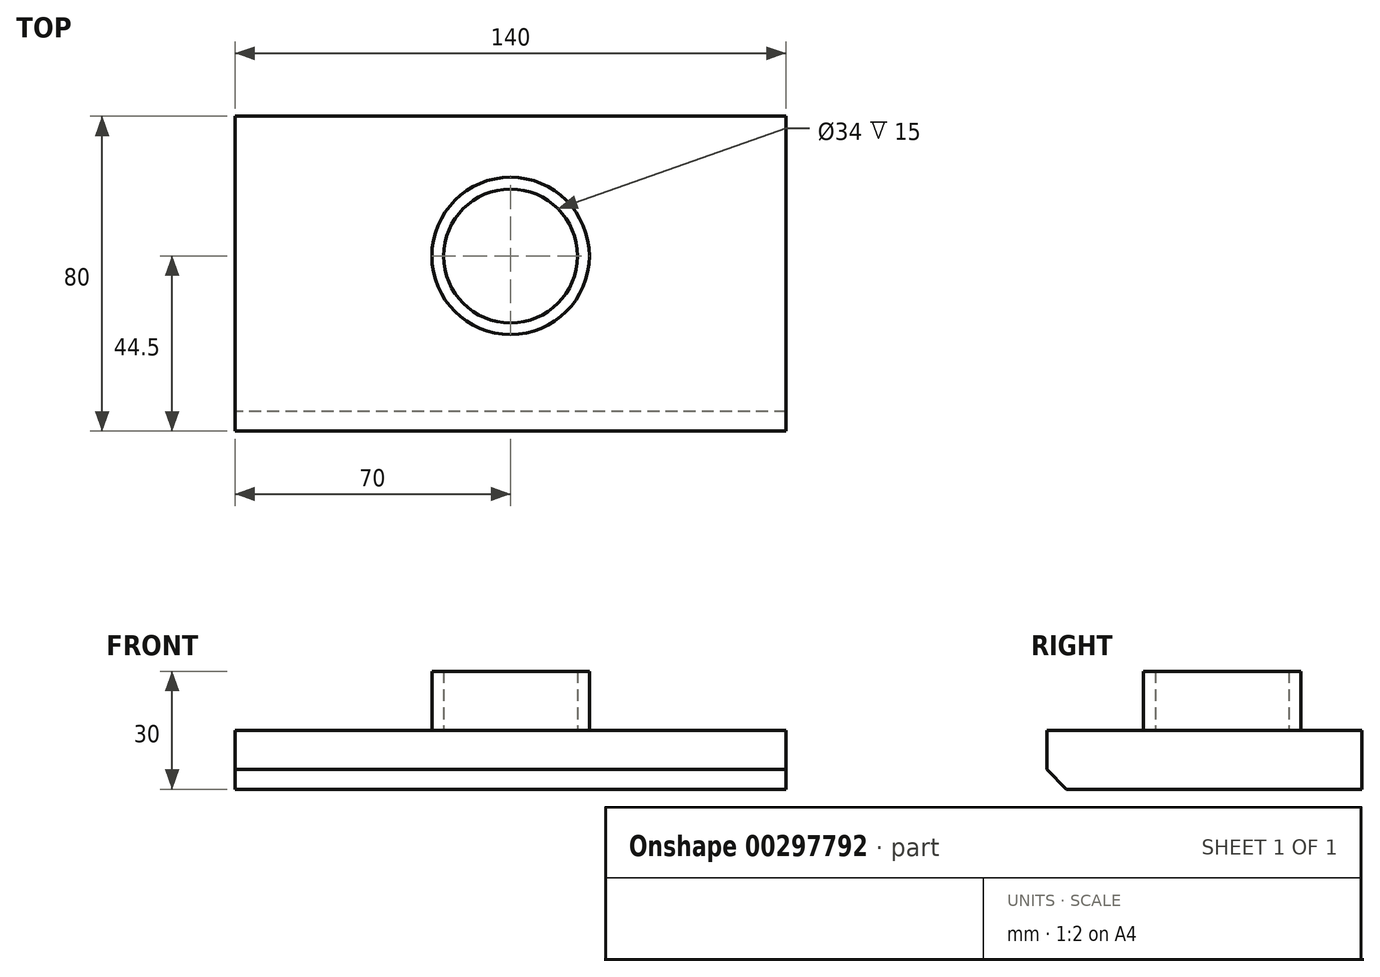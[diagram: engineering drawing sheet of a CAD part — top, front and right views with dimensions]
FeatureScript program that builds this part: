
annotation { "Feature Type Name" : "Feature", "Feature Type Description" : "" }
export const myFeature = defineFeature(function(context is Context, id is Id, definition is map)
    precondition{}
    {
        {
            var Q0;
            Q0=qCreatedBy(makeId("Top.planeOp"),FACE);
            var sketch = newSketch(context, id + "F0", { "sketchPlane" : qUnion([Q0])});
            skLineSegment(sketch, "E0.bottom", {"start": v(70, 40) * mm, "end": v(-70, 40) * mm});
            skLineSegment(sketch, "E0.top", {"start": v(70, -40) * mm, "end": v(-70, -40) * mm});
            skLineSegment(sketch, "E0.left", {"start": v(70, 40) * mm, "end": v(70, -40) * mm});
            skLineSegment(sketch, "E0.right", {"start": v(-70, 40) * mm, "end": v(-70, -40) * mm});
            skPoint(sketch, "E0.middle", {"position": v(0, 0) * mm});
            skSolve(sketch);
        }
        {
            var Q0;
            Q0 = qSketchRegion(id + "F0", true);
            extrude(context, id + "F1", {"entities" : qUnion([Q0]), "depth" : 15 * mm});
        }
        {
            var Q0;
            Q0=makeQuery(id+"F1.opExtrude","CAP_EDGE",EDGE,{"disambiguationData":[OSD([sQuery(id+"F0.wireOp",EDGE,"E0.top")])],"isStart":true});
            chamfer(context, id + "F2", {"entities" : qUnion([Q0]), "width" : 5 * mm, "tangentPropagation" : true});
        }
        {
            var Q0;
            Q0=makeQuery(id+"F1.opExtrude","CAP_FACE",FACE,{"disambiguationData":[OSD([sQuery(id+"F0.wireOp",EDGE,"E0.bottom"),sQuery(id+"F0.wireOp",EDGE,"E0.top"),sQuery(id+"F0.wireOp",EDGE,"E0.left"),sQuery(id+"F0.wireOp",EDGE,"E0.right")])],"isStart":false});
            var sketch = newSketch(context, id + "F3", { "sketchPlane" : qUnion([Q0])});
            skLineSegment(sketch, "E1", {"start": v(0, -40) * mm, "end": v(0, 40) * mm, "construction": true});
            skCircle(sketch, "E2", {"center": v(0, 4.5) * mm, "radius": 20 * mm});
            skCircle(sketch, "E3", {"center": v(0, 4.5) * mm, "radius": 17 * mm});
            skSolve(sketch);
        }
        {
            var Q0;
            Q0 = qSketchRegion(id + "F3", true);
            extrude(context, id + "F4", {"entities" : qUnion([Q0]), "offsetDistance" : 25 * mm, "depth" : 15 * mm});
        }
    });
